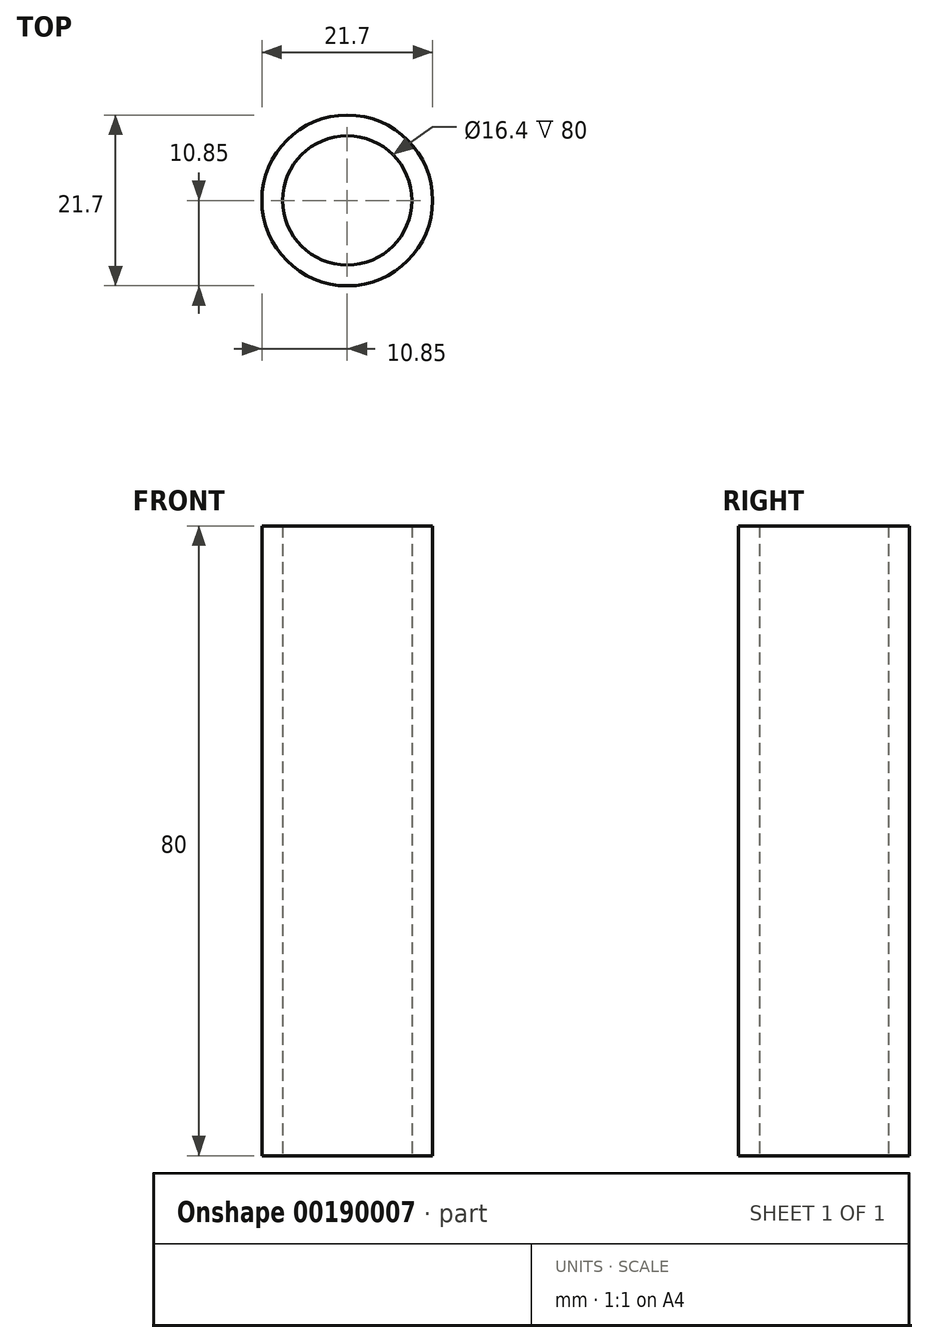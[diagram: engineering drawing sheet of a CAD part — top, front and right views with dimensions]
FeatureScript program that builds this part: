
annotation { "Feature Type Name" : "Feature", "Feature Type Description" : "" }
export const myFeature = defineFeature(function(context is Context, id is Id, definition is map)
    precondition{}
    {
        {
            var Q0;
            Q0=qCreatedBy(makeId("Top.planeOp"),FACE);
            var sketch = newSketch(context, id + "F0", { "sketchPlane" : qUnion([Q0])});
            skCircle(sketch, "E0", {"center": v(0, 0) * mm, "radius": 10.85 * mm});
            skCircle(sketch, "E1.0", {"center": v(0, 0) * mm, "radius": 8.2 * mm});
            skSolve(sketch);
        }
        {
            var Q0;
            Q0 = qSketchRegion(id + "F0", true);
            extrude(context, id + "F1", {"entities" : qUnion([Q0]), "depth" : 80 * mm});
        }
    });
